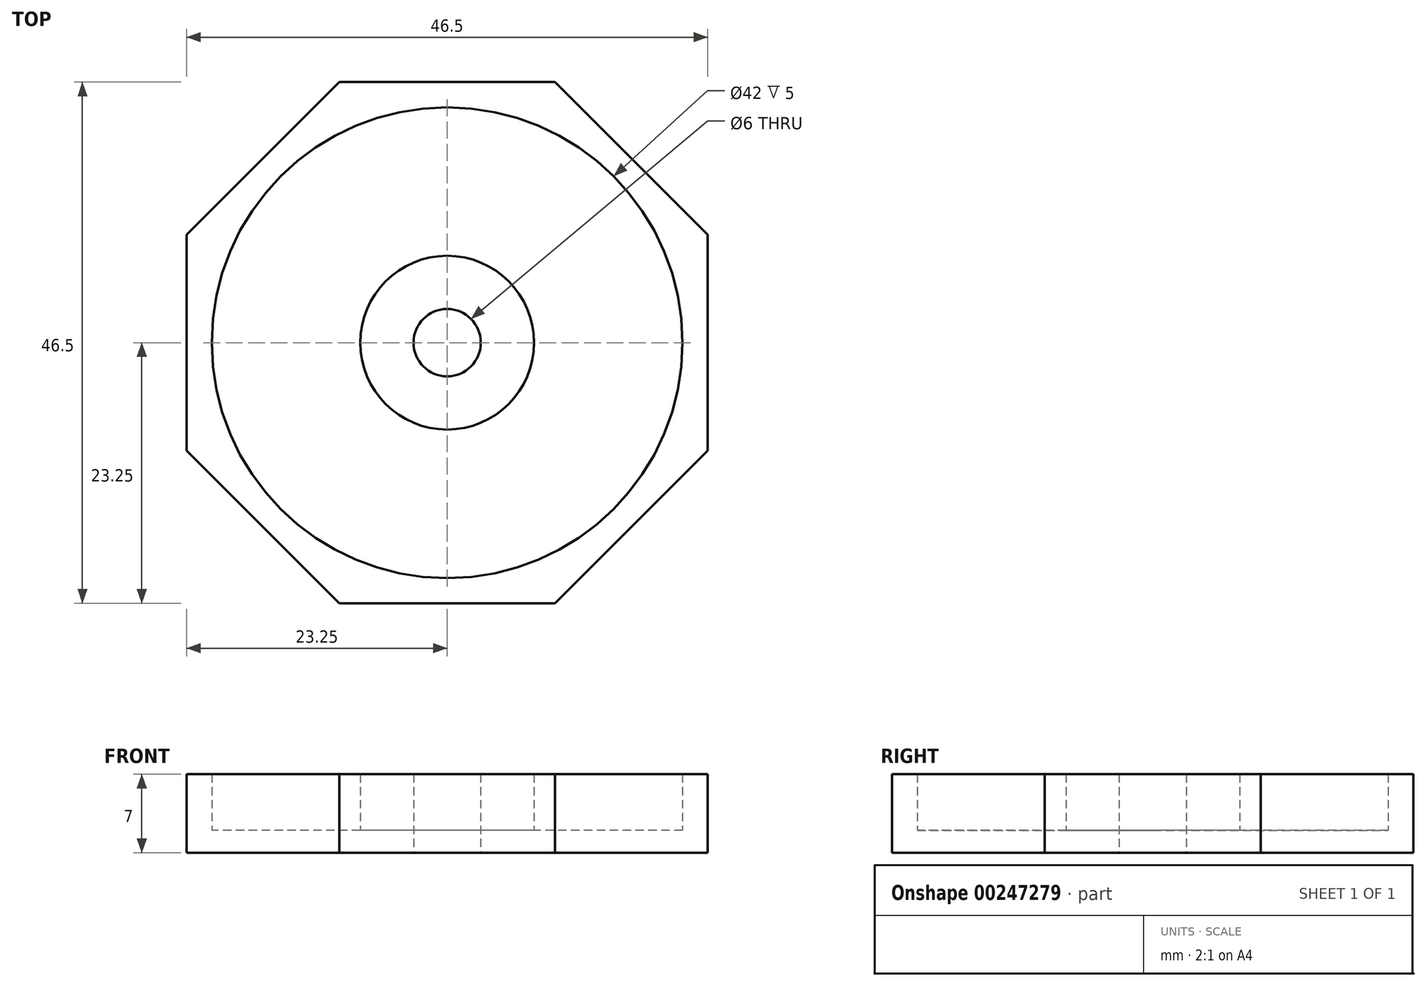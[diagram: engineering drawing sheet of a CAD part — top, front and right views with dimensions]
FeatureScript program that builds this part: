
annotation { "Feature Type Name" : "Feature", "Feature Type Description" : "" }
export const myFeature = defineFeature(function(context is Context, id is Id, definition is map)
    precondition{}
    {
        {
            var Q0;
            Q0=qCreatedBy(makeId("Top.planeOp"),FACE);
            var sketch = newSketch(context, id + "F2", { "sketchPlane" : qUnion([Q0])});
            skCircle(sketch, "E0.cCircle", {"center": v(0, 0) * mm, "radius": 23.25 * mm, "construction": true});
            skLineSegment(sketch, "E0.0", {"start": v(23.25, 9.63) * mm, "end": v(23.25, -9.63) * mm});
            skLineSegment(sketch, "E0.1", {"start": v(23.25, -9.63) * mm, "end": v(9.63, -23.25) * mm});
            skLineSegment(sketch, "E0.2", {"start": v(9.63, -23.25) * mm, "end": v(-9.63, -23.25) * mm});
            skLineSegment(sketch, "E0.3", {"start": v(-9.63, -23.25) * mm, "end": v(-23.25, -9.63) * mm});
            skLineSegment(sketch, "E0.4", {"start": v(-23.25, -9.63) * mm, "end": v(-23.25, 9.63) * mm});
            skLineSegment(sketch, "E0.5", {"start": v(-23.25, 9.63) * mm, "end": v(-9.63, 23.25) * mm});
            skLineSegment(sketch, "E0.6", {"start": v(-9.63, 23.25) * mm, "end": v(9.63, 23.25) * mm});
            skLineSegment(sketch, "E0.7", {"start": v(9.63, 23.25) * mm, "end": v(23.25, 9.63) * mm});
            skPoint(sketch, "E0.0.midPoint", {"position": v(23.25, 0) * mm});
            skCircle(sketch, "E1", {"center": v(0, 0) * mm, "radius": 21 * mm});
            skCircle(sketch, "E2", {"center": v(0, 0) * mm, "radius": 7.75 * mm});
            skCircle(sketch, "E3", {"center": v(0, 0) * mm, "radius": 3 * mm});
            skSolve(sketch);
        }
        {
            var Q0;
            Q0=makeQuery(id+"F2.imprint","IMPRINT",FACE,{"disambiguationData":[TD([[makeQuery(id+"F2.imprint","IMPRINT",EDGE,{"derivedFrom":sQuery(id+"F2.wireOp",EDGE,"E0.0")}),-1.0]])]});
            var Q1;
            Q1=makeQuery(id+"F2.imprint","IMPRINT",FACE,{"disambiguationData":[TD([[makeQuery(id+"F2.imprint","IMPRINT",EDGE,{"derivedFrom":sQuery(id+"F2.wireOp",EDGE,"E2")}),1.0]])]});
            extrude(context, id + "F0", {"entities" : qUnion([Q0, Q1]), "depth" : 7 * mm});
        }
        {
            var Q0;
            Q0=makeQuery(id+"F2.imprint","IMPRINT",FACE,{"disambiguationData":[TD([[makeQuery(id+"F2.imprint","IMPRINT",EDGE,{"derivedFrom":sQuery(id+"F2.wireOp",EDGE,"E1")}),1.0]])]});
            extrude(context, id + "F1", {"entities" : qUnion([Q0]), "operationType" : NewBodyOperationType.ADD, "depth" : 2 * mm});
        }
    });
